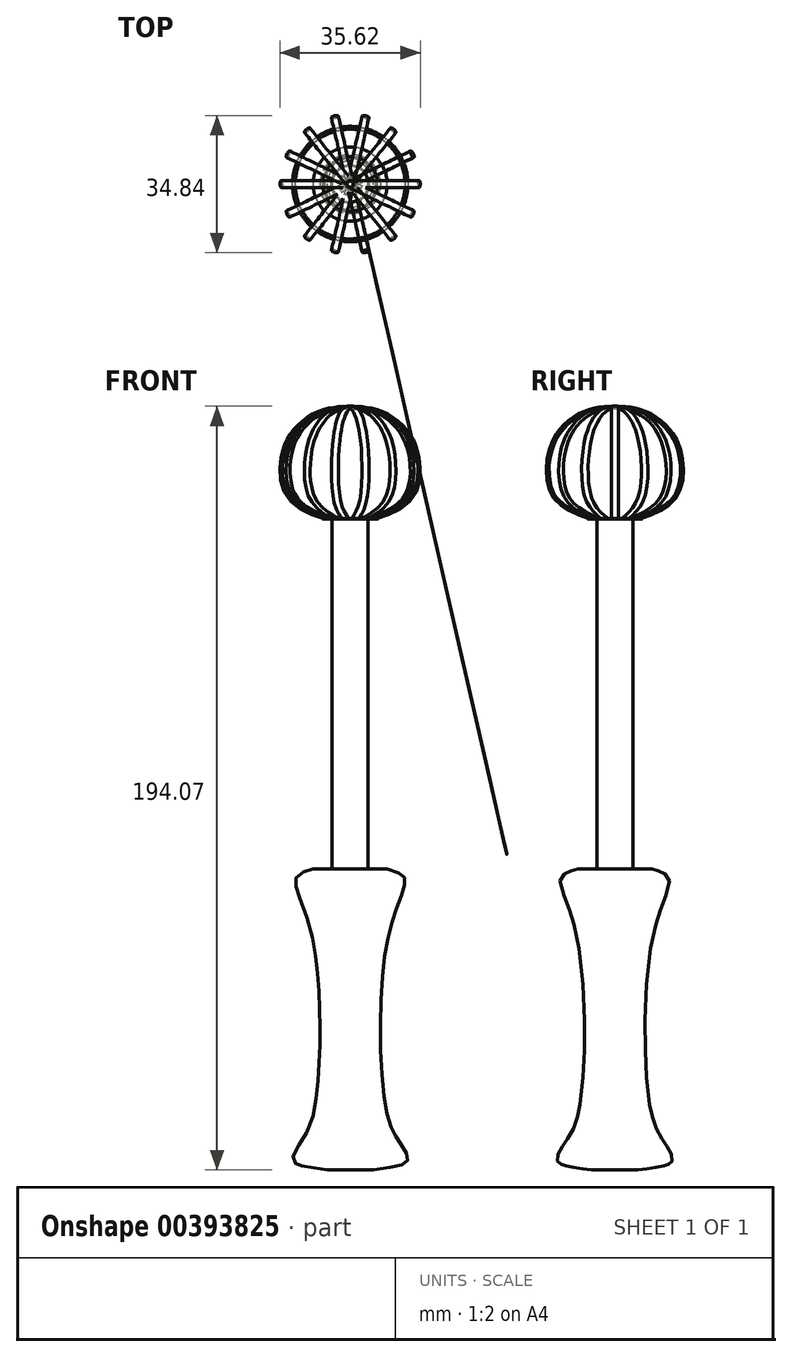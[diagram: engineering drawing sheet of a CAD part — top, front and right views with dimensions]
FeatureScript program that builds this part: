
annotation { "Feature Type Name" : "Feature", "Feature Type Description" : "" }
export const myFeature = defineFeature(function(context is Context, id is Id, definition is map)
    precondition{}
    {
        {
            var Q0;
            Q0=qCreatedBy(makeId("Front.planeOp"),FACE);
            var sketch = newSketch(context, id + "F0", { "sketchPlane" : qUnion([Q0])});
            skFitSpline(sketch, "E0.MirrorCS", {"points": [v(9.41, 0) * mm, v(13.88, -2.59) * mm, v(11.77, -9.88) * mm, v(8, -29.89) * mm, v(9.41, -62.6) * mm, v(12.7, -69.66) * mm, v(14.6, -74.13) * mm, v(5.88, -76.48) * mm], "startDerivative": vector(83.07, -25.34) * mm, "endDerivative": vector(-108.09, -17.6) * mm});
            skLineSegment(sketch, "E1.MirrorCS", {"start": v(0, 0) * mm, "end": v(9.41, 0) * mm});
            skLineSegment(sketch, "E2.MirrorCS", {"start": v(5.88, -76.48) * mm, "end": v(0, -76.48) * mm});
            skPoint(sketch, "E3.2.internal.orphan", {"position": v(-9.41, -12) * mm});
            skPoint(sketch, "E3.5.internal.orphan", {"position": v(-9.41, -69.66) * mm});
            skPoint(sketch, "E4.end.orphan", {"position": v(0, -76.48) * mm});
            skPoint(sketch, "E4.start.orphan", {"position": v(-5.88, -76.48) * mm});
            skPoint(sketch, "E5.end.orphan", {"position": v(-9.41, 0) * mm});
            skPoint(sketch, "E5.start.orphan", {"position": v(0, 0) * mm});
            skLineSegment(sketch, "E6", {"start": v(0, 50.83) * mm, "end": v(0, 8.94) * mm, "construction": true});
            skLineSegment(sketch, "E7", {"start": v(0, 0) * mm, "end": v(0, -76.48) * mm});
            skSolve(sketch);
        }
        {
            var Q0;
            Q0 = qSketchRegion(id + "F0", true);
            var Q1;
            Q1=sQuery(id+"F0.wireOp",EDGE,"E6");
            revolve(context, id + "F1", {"entities" : qUnion([Q0]), "axis" : qUnion([Q1]), "revolveType" : RevolveType.FULL});
        }
        {
            var Q0;
            Q0=qCreatedBy(makeId("Top.planeOp"),FACE);
            var sketch = newSketch(context, id + "F2", { "sketchPlane" : qUnion([Q0])});
            skCircle(sketch, "E8", {"center": v(0, 0) * mm, "radius": 4.57 * mm});
            skSolve(sketch);
        }
        {
            var Q0;
            Q0=makeQuery(id+"F2.imprint","IMPRINT",FACE,{"disambiguationData":[TD([[makeQuery(id+"F2.imprint","IMPRINT",EDGE,{"derivedFrom":sQuery(id+"F2.wireOp",EDGE,"E8")}),1.0]])]});
            extrude(context, id + "F3", {"entities" : qUnion([Q0]), "operationType" : NewBodyOperationType.ADD, "depth" : 88.9 * mm});
        }
        {
            var Q0;
            Q0=makeQuery(id+"F3.opExtrude","CAP_FACE",FACE,{"disambiguationData":[OSD([sQuery(id+"F2.wireOp",EDGE,"E8")])],"isStart":false});
            var sketch = newSketch(context, id + "F4", { "sketchPlane" : qUnion([Q0])});
            skCircle(sketch, "E9", {"center": v(0, 0) * mm, "radius": 6.99 * mm});
            skSolve(sketch);
        }
        {
            var Q0;
            Q0=makeQuery(id+"F4.imprint","IMPRINT",FACE,{"disambiguationData":[TD([[makeQuery(id+"F4.imprint","IMPRINT",EDGE,{"derivedFrom":sQuery(id+"F4.wireOp",EDGE,"E9")}),1.0]])]});
            extrude(context, id + "F5", {"entities" : qUnion([Q0]), "depth" : 0.08 * mm});
        }
        {
            var Q0;
            Q0=makeQuery(id+"F3.opExtrude","CAP_FACE",FACE,{"disambiguationData":[OSD([sQuery(id+"F2.wireOp",EDGE,"E8")])],"isStart":false});
            var sketch = newSketch(context, id + "F6", { "sketchPlane" : qUnion([Q0])});
            skSolve(sketch);
        }
        {
            var Q0;
            Q0=qCreatedBy(makeId("Front.planeOp"),FACE);
            var sketch = newSketch(context, id + "F7", { "sketchPlane" : qUnion([Q0])});
            skLineSegment(sketch, "E10", {"start": v(0, -70.81) * mm, "end": v(0, 184.05) * mm});
            skSolve(sketch);
        }
        {
            var Q0;
            Q0=makeQuery(id+"F6.imprint","IMPRINT",FACE,{"disambiguationData":[TD([[makeQuery(id+"F6.imprint","IMPRINT",EDGE,{"derivedFrom":makeQuery(id+"F3.opExtrude","CAP_EDGE",EDGE,{"disambiguationData":[OSD([sQuery(id+"F2.wireOp",EDGE,"E8")])],"isStart":false})}),1.0]])]});
            var sketch = newSketch(context, id + "F8", { "sketchPlane" : qUnion([Q0])});
            skCircle(sketch, "E11", {"center": v(-5.68, 0) * mm, "radius": 0.9 * mm});
            skSolve(sketch);
        }
        {
            var Q0;
            Q0=qCreatedBy(makeId("Front.planeOp"),FACE);
            var sketch = newSketch(context, id + "F9", { "sketchPlane" : qUnion([Q0])});
            skFitSpline(sketch, "E12", {"points": [v(-5.7, 89.04) * mm, v(-15.77, 94.93) * mm, v(-16.84, 105.56) * mm, v(-13.15, 112.3) * mm, v(-7.51, 116) * mm, v(-2.27, 117.05) * mm, v(0, 117.14) * mm], "startDerivative": vector(-56.4, 19.92) * mm, "endDerivative": vector(21.4, 0.36) * mm});
            skSolve(sketch);
        }
        {
            var Q0;
            Q0 = qSketchRegion(id + "F8", true);
            var Q1;
            Q1=sQuery(id+"F9.wireOp",EDGE,"E12");
            sweep(context, id + "F10", {"profiles" : qUnion([Q0]), "path" : qUnion([Q1])});
        }
        {
            var Q0;
            Q0=makeQuery(id+"F10.opSweep","SWEPT_BODY",BODY,{"disambiguationData":[OSD([sQuery(id+"F8.wireOp",EDGE,"E11"),sQuery(id+"F9.wireOp",EDGE,"E12")])]});
            var Q1;
            Q1=sQuery(id+"F7.wireOp",EDGE,"E10");
            circularPattern(context, id + "F11", {"entities" : qUnion([Q0]), "axis" : qUnion([Q1]), "angle" : 360 * degree, "instanceCount" : 14, "equalSpace" : true});
        }
    });
